# Revit family: Accessory-Touchless-Soap_Dispenser-KOHLER-Curve-K-25197_1
name_source: partatom
category: Specialty Equipment
revit_build: Autodesk Revit 2017 (Build: 20160225_1515(x64)
units: mm (PartAtom-declared; Revit-internal decimal feet)

## family parameters
Cut with Voids When Loaded = No
Host = Face
OmniClass Number = 23.31.25.29.13
OmniClass Title = Hand Soap Dispensers
Part Type = Normal
Room Calculation Point = No
Round Connector Dimension = Use Diameter
Shared = No

## types (1)
- CP-Polished Chrome
    ADA Compliant = No
    Apparent Load = 0 VA
    Assembly Code = C1030200
    Date Modified = 08/14/2020
    Default Elevation = 42"
    Description = Foam Soap Dispenser-AC
    Electrical Connector = Yes
    Electrical Note = One Dedicated Circuit Required, Protected With Class A Ground-Fault Circuit-Interrupter (GFCI). Outside North America,
This Device May Be Known As a Residual Current Device (RCD).
    Finish = Kohler-Metal-CP-Polished_Chrome
    Height = 3 1/2"
    Length = 5 5/8"
    Manufacturer = KOHLER Co.
    Master Format 2014 = 10 28 00
    Master Format 2014 Name = Toilet, Bath, and Laundry Accessories
    Material = Cast Brass Construction
    Model = K-25197-CP
    Product Documentation Link = https://www.us.kohler.com
    Product Name = Curve
    Product Page URL = http://www.us.kohler.com
    Type = 1
    URL = https://www.us.kohler.com
    Voltage = 120 V
    WaterSense Certified = No
    Width = 1 13/16"

## geometry (parser evidence)
native form markers: Sweep x6
no freeform markers — native parametric forms only
